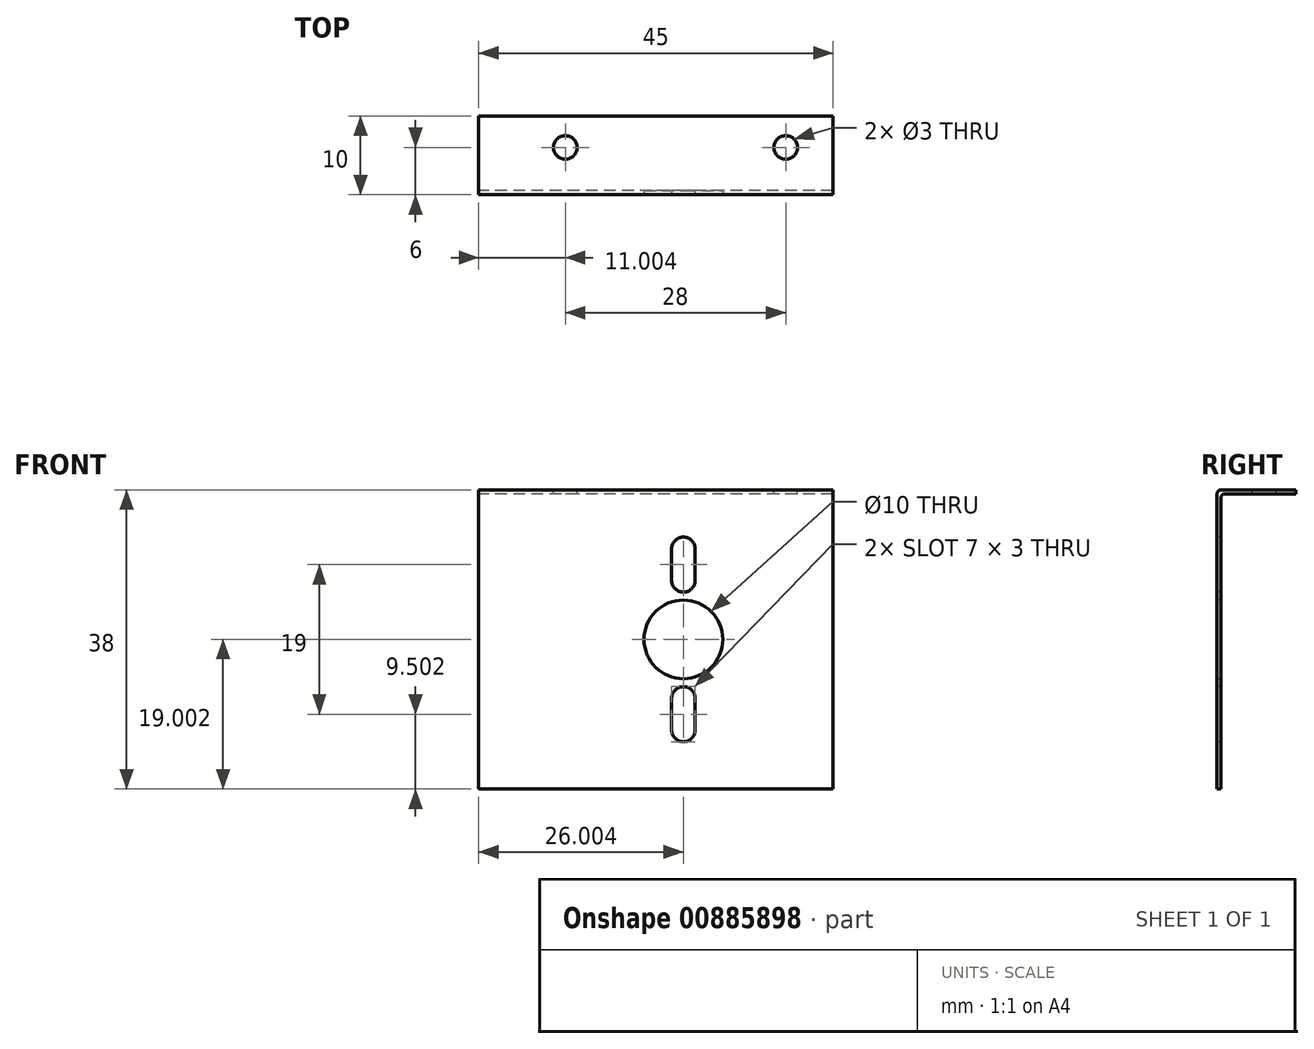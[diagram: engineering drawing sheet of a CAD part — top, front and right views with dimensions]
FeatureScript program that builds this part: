
annotation { "Feature Type Name" : "Feature", "Feature Type Description" : "" }
export const myFeature = defineFeature(function(context is Context, id is Id, definition is map)
    precondition{}
    {
        {
            var Q0;
            Q0=qCreatedBy(makeId("Front.planeOp"),FACE);
            var sketch = newSketch(context, id + "F0", { "sketchPlane" : qUnion([Q0])});
            skLineSegment(sketch, "E0.bottom", {"start": v(-13.07, 17.28) * mm, "end": v(31.93, 17.28) * mm});
            skLineSegment(sketch, "E0.top", {"start": v(-13.07, -20.72) * mm, "end": v(31.93, -20.72) * mm});
            skLineSegment(sketch, "E0.left", {"start": v(-13.07, 17.28) * mm, "end": v(-13.07, -20.72) * mm});
            skLineSegment(sketch, "E0.right", {"start": v(31.93, 17.28) * mm, "end": v(31.93, -20.72) * mm});
            skSolve(sketch);
        }
        {
            var Q0;
            Q0 = qSketchRegion(id + "F0", true);
            extrude(context, id + "F1", {"entities" : qUnion([Q0]), "depth" : 0.5 * mm, "offsetDistance" : 25 * mm});
        }
        {
            var Q0;
            Q0=makeQuery(id+"F1.opExtrude","SWEPT_FACE",FACE,{"disambiguationData":[OSD([sQuery(id+"F0.wireOp",EDGE,"E0.bottom")])]});
            var sketch = newSketch(context, id + "F2", { "sketchPlane" : qUnion([Q0])});
            skLineSegment(sketch, "E1.bottom", {"start": v(31.93, -0.5) * mm, "end": v(-13.07, -0.5) * mm});
            skLineSegment(sketch, "E1.top", {"start": v(31.93, 9.5) * mm, "end": v(-13.07, 9.5) * mm});
            skLineSegment(sketch, "E1.left", {"start": v(31.93, -0.5) * mm, "end": v(31.93, 9.5) * mm});
            skLineSegment(sketch, "E1.right", {"start": v(-13.07, -0.5) * mm, "end": v(-13.07, 9.5) * mm});
            skCircle(sketch, "E2", {"center": v(-2.07, 5.5) * mm, "radius": 1.5 * mm});
            skCircle(sketch, "E3", {"center": v(25.93, 5.5) * mm, "radius": 1.5 * mm});
            skSolve(sketch);
        }
        {
            var Q0;
            Q0 = qSketchRegion(id + "F2", true);
            extrude(context, id + "F3", {"entities" : qUnion([Q0]), "operationType" : NewBodyOperationType.ADD, "oppositeDirection" : true, "depth" : 0.5 * mm, "offsetDistance" : 25 * mm});
        }
        {
            var Q0;
            Q0=makeQuery(id+"F1.opExtrude","CAP_EDGE",EDGE,{"disambiguationData":[OSD([sQuery(id+"F0.wireOp",EDGE,"E0.bottom")])],"isStart":false});
            var Q1;
            Q1=makeQuery(id+"F3.boolean.opBoolean","INTERSECT",EDGE,{"derivedFrom":[makeQuery(id+"F1.opExtrude","CAP_FACE",FACE,{"disambiguationData":[OSD([sQuery(id+"F0.wireOp",EDGE,"E0.bottom"),sQuery(id+"F0.wireOp",EDGE,"E0.top"),sQuery(id+"F0.wireOp",EDGE,"E0.left"),sQuery(id+"F0.wireOp",EDGE,"E0.right")])],"isStart":true}),makeQuery(id+"F3.opExtrude","CAP_FACE",FACE,{"disambiguationData":[OSD([sQuery(id+"F2.wireOp",EDGE,"E1.bottom"),sQuery(id+"F2.wireOp",EDGE,"E1.top"),sQuery(id+"F2.wireOp",EDGE,"E1.left"),sQuery(id+"F2.wireOp",EDGE,"E1.right"),sQuery(id+"F2.wireOp",EDGE,"E2"),sQuery(id+"F2.wireOp",EDGE,"E3")])],"isStart":false})]});
            fillet(context, id + "F4", {"entities" : qUnion([Q0, Q1]), "radius" : 0.5 * mm, "tangentPropagation" : true, "allowEdgeOverflow" : false});
        }
        {
            var Q0;
            Q0=makeQuery(id+"F1.opExtrude","CAP_FACE",FACE,{"disambiguationData":[OSD([sQuery(id+"F0.wireOp",EDGE,"E0.bottom"),sQuery(id+"F0.wireOp",EDGE,"E0.top"),sQuery(id+"F0.wireOp",EDGE,"E0.left"),sQuery(id+"F0.wireOp",EDGE,"E0.right")])],"isStart":false});
            var sketch = newSketch(context, id + "F5", { "sketchPlane" : qUnion([Q0])});
            skCircle(sketch, "E4", {"center": v(12.93, -1.72) * mm, "radius": 5 * mm});
            skLineSegment(sketch, "E5", {"start": v(12.93, -22.26) * mm, "end": v(12.93, 18.83) * mm, "construction": true});
            skArc(sketch, "E6", {"start": v(14.43, 9.78) * mm, "mid": v(12.93, 11.28) * mm, "end": v(11.43, 9.78) * mm});
            skArc(sketch, "E7", {"start": v(11.43, 5.78) * mm, "mid": v(12.93, 4.28) * mm, "end": v(14.43, 5.78) * mm});
            skArc(sketch, "E8", {"start": v(14.43, -9.22) * mm, "mid": v(12.93, -7.72) * mm, "end": v(11.43, -9.22) * mm});
            skArc(sketch, "E9", {"start": v(11.43, -13.22) * mm, "mid": v(12.93, -14.72) * mm, "end": v(14.43, -13.22) * mm});
            skLineSegment(sketch, "E10", {"start": v(11.43, -9.22) * mm, "end": v(11.43, -13.22) * mm});
            skLineSegment(sketch, "E11", {"start": v(14.43, -9.22) * mm, "end": v(14.43, -13.22) * mm});
            skLineSegment(sketch, "E12", {"start": v(11.43, 9.78) * mm, "end": v(11.43, 5.78) * mm});
            skLineSegment(sketch, "E13", {"start": v(14.43, 9.78) * mm, "end": v(14.43, 5.78) * mm});
            skSolve(sketch);
        }
        {
            var Q0;
            Q0 = qSketchRegion(id + "F5", true);
            extrude(context, id + "F6", {"entities" : qUnion([Q0]), "operationType" : NewBodyOperationType.REMOVE, "oppositeDirection" : true, "depth" : 25 * mm, "offsetDistance" : 25 * mm});
        }
    });
